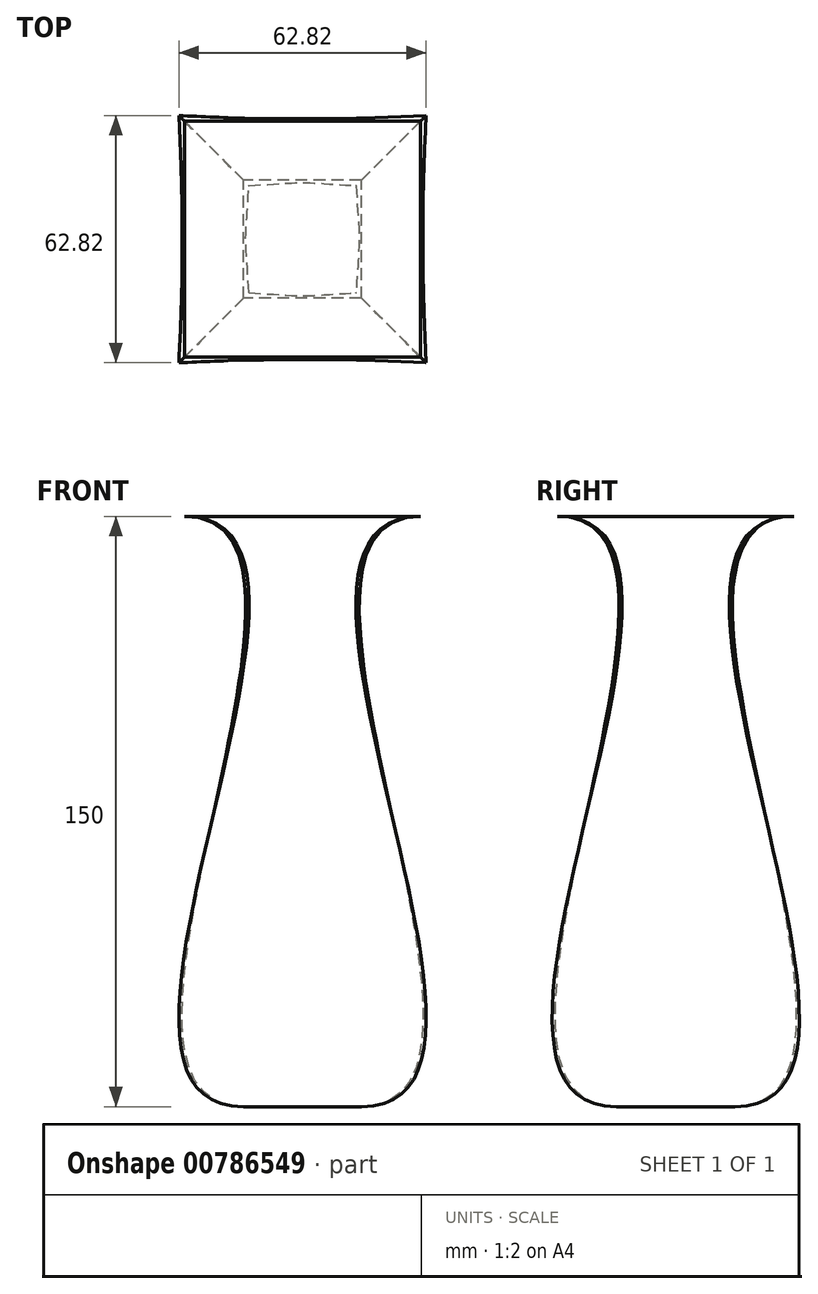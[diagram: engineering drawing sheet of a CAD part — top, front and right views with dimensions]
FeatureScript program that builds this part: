
annotation { "Feature Type Name" : "Feature", "Feature Type Description" : "" }
export const myFeature = defineFeature(function(context is Context, id is Id, definition is map)
    precondition{}
    {
        {
            var Q0;
            Q0=qCreatedBy(makeId("Top.planeOp"),FACE);
            var sketch = newSketch(context, id + "F0", { "sketchPlane" : qUnion([Q0])});
            skLineSegment(sketch, "E0.bottom", {"start": v(15, -15) * mm, "end": v(-15, -15) * mm});
            skLineSegment(sketch, "E0.top", {"start": v(15, 15) * mm, "end": v(-15, 15) * mm});
            skLineSegment(sketch, "E0.left", {"start": v(15, -15) * mm, "end": v(15, 15) * mm});
            skLineSegment(sketch, "E0.right", {"start": v(-15, -15) * mm, "end": v(-15, 15) * mm});
            skPoint(sketch, "E0.middle", {"position": v(0, 0) * mm});
            skSolve(sketch);
        }
        {
            var Q0;
            Q0=qCreatedBy(makeId("Top.planeOp"),FACE);
            cPlane(context, id + "F1", {"entities" : qUnion([Q0]), "cplaneType" : CPlaneType.OFFSET, "offset" : 150 * mm, "width" : 150 * mm, "height" : 150 * mm});
        }
        {
            var Q0;
            Q0=qCreatedBy(id+"F1.planeOp",FACE);
            var sketch = newSketch(context, id + "F2", { "sketchPlane" : qUnion([Q0])});
            skLineSegment(sketch, "E1.bottom", {"start": v(30, 30) * mm, "end": v(-30, 30) * mm});
            skLineSegment(sketch, "E1.top", {"start": v(30, -30) * mm, "end": v(-30, -30) * mm});
            skLineSegment(sketch, "E1.left", {"start": v(30, 30) * mm, "end": v(30, -30) * mm});
            skLineSegment(sketch, "E1.right", {"start": v(-30, 30) * mm, "end": v(-30, -30) * mm});
            skPoint(sketch, "E1.middle", {"position": v(0, 0) * mm});
            skSolve(sketch);
        }
        {
            var Q0;
            Q0=makeQuery(id+"F0.imprint","IMPRINT",FACE,{"disambiguationData":[TD([[makeQuery(id+"F0.imprint","IMPRINT",EDGE,{"derivedFrom":sQuery(id+"F0.wireOp",EDGE,"E0.bottom")}),-1.0]])]});
            var Q1;
            Q1=makeQuery(id+"F2.imprint","IMPRINT",FACE,{"disambiguationData":[TD([[makeQuery(id+"F2.imprint","IMPRINT",EDGE,{"derivedFrom":sQuery(id+"F2.wireOp",EDGE,"E1.bottom")}),1.0]])]});
            loft(context, id + "F3", {"startCondition" : LoftEndDerivativeType.TANGENT_TO_PROFILE, "startMagnitude" : 10, "endCondition" : LoftEndDerivativeType.TANGENT_TO_PROFILE, "endMagnitude" : 10, "sheetProfilesArray" : [{ "sheetProfileEntities" : qUnion([Q0]) }, { "sheetProfileEntities" : qUnion([Q1]) }]});
        }
    });
